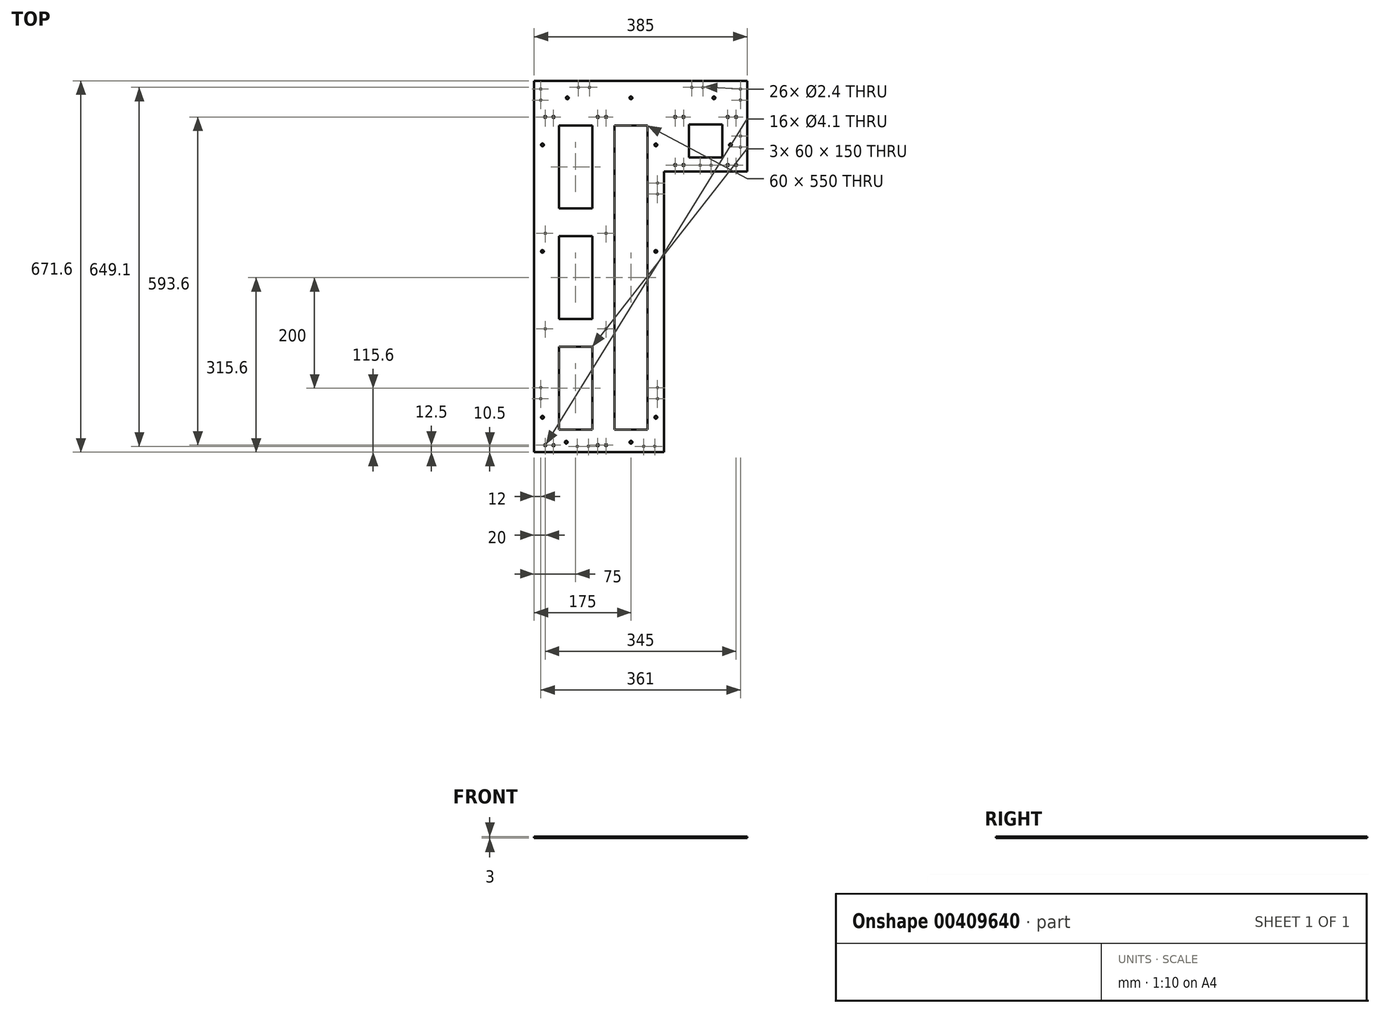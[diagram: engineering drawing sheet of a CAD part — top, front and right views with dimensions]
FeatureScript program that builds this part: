
annotation { "Feature Type Name" : "Feature", "Feature Type Description" : "" }
export const myFeature = defineFeature(function(context is Context, id is Id, definition is map)
    precondition{}
    {
        {
            var Q0;
            Q0=qCreatedBy(makeId("Top.planeOp"),FACE);
            var sketch = newSketch(context, id + "F0", { "sketchPlane" : qUnion([Q0])});
            skLineSegment(sketch, "E0.bottom", {"start": v(192.5, -53) * mm, "end": v(-192.5, -53) * mm});
            skLineSegment(sketch, "E0.top", {"start": v(192.5, 53) * mm, "end": v(-192.5, 53) * mm});
            skLineSegment(sketch, "E0.left", {"start": v(192.5, -53) * mm, "end": v(192.5, 53) * mm});
            skLineSegment(sketch, "E0.right", {"start": v(-192.5, -53) * mm, "end": v(-192.5, 53) * mm});
            skPoint(sketch, "E0.middle", {"position": v(0, 0) * mm});
            skCircle(sketch, "E1", {"center": v(-172.5, 43.5) * mm, "radius": 2.05 * mm});
            skCircle(sketch, "E2", {"center": v(-157.5, 43.5) * mm, "radius": 2.05 * mm});
            skLineSegment(sketch, "E3", {"start": v(-42.5, 73.43) * mm, "end": v(-42.5, -580.65) * mm, "construction": true});
            skLineSegment(sketch, "E4", {"start": v(42.5, 94.16) * mm, "end": v(42.5, -111.22) * mm, "construction": true});
            skCircle(sketch, "E5", {"center": v(-77.5, 43.5) * mm, "radius": 2.05 * mm});
            skCircle(sketch, "E6", {"center": v(-62.5, 43.5) * mm, "radius": 2.05 * mm});
            skCircle(sketch, "E7", {"center": v(62.5, 43.5) * mm, "radius": 2.05 * mm});
            skCircle(sketch, "E8", {"center": v(77.5, 43.5) * mm, "radius": 2.05 * mm});
            skCircle(sketch, "E9", {"center": v(157.5, 43.5) * mm, "radius": 2.05 * mm});
            skCircle(sketch, "E10", {"center": v(172.5, 43.5) * mm, "radius": 2.05 * mm});
            skLineSegment(sketch, "E11", {"start": v(202.9, -33.92) * mm, "end": v(25.15, -33.92) * mm, "construction": true});
            skCircle(sketch, "E12", {"center": v(172.5, -43.42) * mm, "radius": 2.05 * mm});
            skCircle(sketch, "E13", {"center": v(157.5, -43.42) * mm, "radius": 2.05 * mm});
            skCircle(sketch, "E14", {"center": v(62.5, -43.42) * mm, "radius": 2.05 * mm});
            skCircle(sketch, "E15", {"center": v(77.5, -43.42) * mm, "radius": 2.05 * mm});
            skLineSegment(sketch, "E16.bottom", {"start": v(-192.5, -53) * mm, "end": v(42.5, -53) * mm});
            skLineSegment(sketch, "E16.top", {"start": v(-192.5, -559.6) * mm, "end": v(42.5, -559.6) * mm});
            skLineSegment(sketch, "E16.left", {"start": v(-192.5, -53) * mm, "end": v(-192.5, -559.6) * mm});
            skLineSegment(sketch, "E16.right", {"start": v(42.5, -53) * mm, "end": v(42.5, -559.6) * mm});
            skLineSegment(sketch, "E17", {"start": v(-218.51, -539.6) * mm, "end": v(119.99, -539.6) * mm, "construction": true});
            skCircle(sketch, "E18", {"center": v(-172.5, -550.1) * mm, "radius": 2.05 * mm});
            skCircle(sketch, "E19", {"center": v(-157.5, -550.1) * mm, "radius": 2.05 * mm});
            skCircle(sketch, "E20", {"center": v(-77.5, -550.1) * mm, "radius": 2.05 * mm});
            skCircle(sketch, "E21", {"center": v(-62.5, -550.1) * mm, "radius": 2.05 * mm});
            skLineSegment(sketch, "E22", {"start": v(-117.5, 57.85) * mm, "end": v(-117.5, 33.54) * mm, "construction": true});
            skLineSegment(sketch, "E23", {"start": v(-153.12, 33) * mm, "end": v(-174.42, 33) * mm, "construction": true});
            skCircle(sketch, "E24", {"center": v(-172.5, -167) * mm, "radius": 1.2 * mm});
            skLineSegment(sketch, "E25", {"start": v(-176.5, -137.08) * mm, "end": v(-176.5, -144.67) * mm, "construction": true});
            skCircle(sketch, "E26", {"center": v(-172.5, -339.6) * mm, "radius": 1.2 * mm});
            skCircle(sketch, "E27", {"center": v(-62.5, -167) * mm, "radius": 1.2 * mm});
            skCircle(sketch, "E28", {"center": v(-62.5, -339.6) * mm, "radius": 1.2 * mm});
            skCircle(sketch, "E29", {"center": v(-177.5, -199.6) * mm, "radius": 2.5 * mm});
            skCircle(sketch, "E30", {"center": v(-134.5, -544.6) * mm, "radius": 2.5 * mm});
            skLineSegment(sketch, "E31.top", {"start": v(-192.5, -562.6) * mm, "end": v(42.5, -562.6) * mm});
            skLineSegment(sketch, "E31.left", {"start": v(-192.5, -559.6) * mm, "end": v(-192.5, -562.6) * mm});
            skLineSegment(sketch, "E31.right", {"start": v(42.5, -559.6) * mm, "end": v(42.5, -562.6) * mm});
            skCircle(sketch, "E32", {"center": v(-177.5, -499.6) * mm, "radius": 2.5 * mm});
            skCircle(sketch, "E33", {"center": v(-177.5, -7) * mm, "radius": 2.5 * mm});
            skCircle(sketch, "E34", {"center": v(27.5, -199.6) * mm, "radius": 2.5 * mm});
            skCircle(sketch, "E35", {"center": v(-17.5, -544.6) * mm, "radius": 2.5 * mm});
            skCircle(sketch, "E36", {"center": v(27.5, -499.6) * mm, "radius": 2.5 * mm});
            skCircle(sketch, "E37", {"center": v(27.5, -7) * mm, "radius": 2.5 * mm});
            skCircle(sketch, "E38", {"center": v(-132.5, 78) * mm, "radius": 2.5 * mm});
            skCircle(sketch, "E39", {"center": v(132.5, 78) * mm, "radius": 2.5 * mm});
            skCircle(sketch, "E40", {"center": v(-17.5, 78) * mm, "radius": 2.5 * mm});
            skLineSegment(sketch, "E41.bottom", {"start": v(42.5, -53) * mm, "end": v(192.5, -53) * mm});
            skLineSegment(sketch, "E41.top", {"start": v(42.5, -55) * mm, "end": v(192.5, -55) * mm});
            skLineSegment(sketch, "E41.left", {"start": v(42.5, -53) * mm, "end": v(42.5, -55) * mm});
            skLineSegment(sketch, "E41.right", {"start": v(192.5, -53) * mm, "end": v(192.5, -55) * mm});
            skLineSegment(sketch, "E42", {"start": v(-192.5, 53) * mm, "end": v(-192.5, 109) * mm});
            skLineSegment(sketch, "E43", {"start": v(-192.5, 109) * mm, "end": v(192.5, 109) * mm});
            skLineSegment(sketch, "E44", {"start": v(192.5, 109) * mm, "end": v(192.5, 53) * mm});
            skCircle(sketch, "E45", {"center": v(162.5, -7) * mm, "radius": 2.5 * mm});
            skSolve(sketch);
        }
        {
            var Q0;
            Q0 = qSketchRegion(id + "F0", true);
            extrude(context, id + "F1", {"entities" : qUnion([Q0]), "depth" : 3 * mm});
        }
        {
            var Q0;
            Q0=makeQuery(id+"F1.opExtrude","CAP_FACE",FACE,{"disambiguationData":[OSD([sQuery(id+"F0.wireOp",EDGE,"E0.bottom"),sQuery(id+"F0.wireOp",EDGE,"E0.top"),sQuery(id+"F0.wireOp",EDGE,"E0.left"),sQuery(id+"F0.wireOp",EDGE,"E0.right"),sQuery(id+"F0.wireOp",EDGE,"E1"),sQuery(id+"F0.wireOp",EDGE,"E2"),sQuery(id+"F0.wireOp",EDGE,"E5"),sQuery(id+"F0.wireOp",EDGE,"E6"),sQuery(id+"F0.wireOp",EDGE,"E7"),sQuery(id+"F0.wireOp",EDGE,"E8"),sQuery(id+"F0.wireOp",EDGE,"E9"),sQuery(id+"F0.wireOp",EDGE,"E10"),sQuery(id+"F0.wireOp",EDGE,"E12"),sQuery(id+"F0.wireOp",EDGE,"E13"),sQuery(id+"F0.wireOp",EDGE,"E14"),sQuery(id+"F0.wireOp",EDGE,"E15"),sQuery(id+"F0.wireOp",EDGE,"E16.top"),sQuery(id+"F0.wireOp",EDGE,"E16.left"),sQuery(id+"F0.wireOp",EDGE,"E16.right"),sQuery(id+"F0.wireOp",EDGE,"E18"),sQuery(id+"F0.wireOp",EDGE,"E19"),sQuery(id+"F0.wireOp",EDGE,"E20"),sQuery(id+"F0.wireOp",EDGE,"E21")])],"isStart":false});
            var sketch = newSketch(context, id + "F2", { "sketchPlane" : qUnion([Q0])});
            skLineSegment(sketch, "E46.bottom", {"start": v(-87.5, -122) * mm, "end": v(-147.5, -122) * mm});
            skLineSegment(sketch, "E46.top", {"start": v(-87.5, 28) * mm, "end": v(-147.5, 28) * mm});
            skLineSegment(sketch, "E46.left", {"start": v(-87.5, -122) * mm, "end": v(-87.5, 28) * mm});
            skLineSegment(sketch, "E46.right", {"start": v(-147.5, -122) * mm, "end": v(-147.5, 28) * mm});
            skPoint(sketch, "E46.middle", {"position": v(-117.5, -47) * mm});
            skLineSegment(sketch, "E47.bottom", {"start": v(-87.5, -172) * mm, "end": v(-147.5, -172) * mm});
            skLineSegment(sketch, "E47.top", {"start": v(-87.5, -322) * mm, "end": v(-147.5, -322) * mm});
            skLineSegment(sketch, "E47.left", {"start": v(-87.5, -172) * mm, "end": v(-87.5, -322) * mm});
            skLineSegment(sketch, "E47.right", {"start": v(-147.5, -172) * mm, "end": v(-147.5, -322) * mm});
            skPoint(sketch, "E47.middle", {"position": v(-117.5, -247) * mm});
            skLineSegment(sketch, "E48", {"start": v(-117.5, 70.25) * mm, "end": v(-117.5, -57.76) * mm, "construction": true});
            skLineSegment(sketch, "E49", {"start": v(117.5, 72.9) * mm, "end": v(117.5, -109.15) * mm, "construction": true});
            skLineSegment(sketch, "E50.bottom", {"start": v(147.5, -30) * mm, "end": v(87.5, -30) * mm});
            skLineSegment(sketch, "E50.top", {"start": v(147.5, 30) * mm, "end": v(87.5, 30) * mm});
            skLineSegment(sketch, "E50.left", {"start": v(147.5, -30) * mm, "end": v(147.5, 30) * mm});
            skLineSegment(sketch, "E50.right", {"start": v(87.5, -30) * mm, "end": v(87.5, 30) * mm});
            skPoint(sketch, "E50.middle", {"position": v(117.5, 0) * mm});
            skLineSegment(sketch, "E51.bottom", {"start": v(-87.5, -372) * mm, "end": v(-147.5, -372) * mm});
            skLineSegment(sketch, "E51.top", {"start": v(-87.5, -522) * mm, "end": v(-147.5, -522) * mm});
            skLineSegment(sketch, "E51.left", {"start": v(-87.5, -372) * mm, "end": v(-87.5, -522) * mm});
            skLineSegment(sketch, "E51.right", {"start": v(-147.5, -372) * mm, "end": v(-147.5, -522) * mm});
            skPoint(sketch, "E51.middle", {"position": v(-117.5, -447) * mm});
            skLineSegment(sketch, "E52", {"start": v(-42.5, 117.64) * mm, "end": v(-42.5, -137.41) * mm, "construction": true});
            skLineSegment(sketch, "E53.bottom", {"start": v(-47.5, 28) * mm, "end": v(12.5, 28) * mm});
            skLineSegment(sketch, "E53.top", {"start": v(-47.5, -522) * mm, "end": v(12.5, -522) * mm});
            skLineSegment(sketch, "E53.left", {"start": v(-47.5, 28) * mm, "end": v(-47.5, -522) * mm});
            skLineSegment(sketch, "E53.right", {"start": v(12.5, 28) * mm, "end": v(12.5, -522) * mm});
            skSolve(sketch);
        }
        {
            var Q0;
            Q0 = qSketchRegion(id + "F2", true);
            extrude(context, id + "F3", {"entities" : qUnion([Q0]), "operationType" : NewBodyOperationType.REMOVE, "oppositeDirection" : true, "depth" : 25 * mm});
        }
        {
            var Q0;
            Q0=makeQuery(id+"F2O8r8H572E9jEw_1.boolean.opBoolean","MERGE",FACE,{"derivedFrom":[makeQuery(id+"F1.opExtrude","CAP_FACE",FACE,{"disambiguationData":[OSD([sQuery(id+"F0.wireOp",EDGE,"E0.top"),sQuery(id+"F0.wireOp",EDGE,"E0.left"),sQuery(id+"F0.wireOp",EDGE,"E0.right"),sQuery(id+"F0.wireOp",EDGE,"E1"),sQuery(id+"F0.wireOp",EDGE,"E2"),sQuery(id+"F0.wireOp",EDGE,"E5"),sQuery(id+"F0.wireOp",EDGE,"E6"),sQuery(id+"F0.wireOp",EDGE,"E7"),sQuery(id+"F0.wireOp",EDGE,"E8"),sQuery(id+"F0.wireOp",EDGE,"E9"),sQuery(id+"F0.wireOp",EDGE,"E10"),sQuery(id+"F0.wireOp",EDGE,"E12"),sQuery(id+"F0.wireOp",EDGE,"E13"),sQuery(id+"F0.wireOp",EDGE,"E14"),sQuery(id+"F0.wireOp",EDGE,"E15"),sQuery(id+"F0.wireOp",EDGE,"E16.left"),sQuery(id+"F0.wireOp",EDGE,"E16.right"),sQuery(id+"F0.wireOp",EDGE,"E18"),sQuery(id+"F0.wireOp",EDGE,"E19"),sQuery(id+"F0.wireOp",EDGE,"E20"),sQuery(id+"F0.wireOp",EDGE,"E21"),sQuery(id+"F0.wireOp",EDGE,"E24"),sQuery(id+"F0.wireOp",EDGE,"E26"),sQuery(id+"F0.wireOp",EDGE,"E27"),sQuery(id+"F0.wireOp",EDGE,"E28"),sQuery(id+"F0.wireOp",EDGE,"E29"),sQuery(id+"F0.wireOp",EDGE,"E30"),sQuery(id+"F0.wireOp",EDGE,"E31.top"),sQuery(id+"F0.wireOp",EDGE,"E31.left"),sQuery(id+"F0.wireOp",EDGE,"E31.right"),sQuery(id+"F0.wireOp",EDGE,"E32"),sQuery(id+"F0.wireOp",EDGE,"E33"),sQuery(id+"F0.wireOp",EDGE,"E34"),sQuery(id+"F0.wireOp",EDGE,"E35"),sQuery(id+"F0.wireOp",EDGE,"E36"),sQuery(id+"F0.wireOp",EDGE,"E37"),sQuery(id+"F0.wireOp",EDGE,"E38"),sQuery(id+"F0.wireOp",EDGE,"E39"),sQuery(id+"F0.wireOp",EDGE,"TjULq03c-Gpqh-KJec-qWmQ-0YuIlEzygd5B"),sQuery(id+"F0.wireOp",EDGE,"lCEzzgQS-Qvkz-X3D3-LDLk-qSDPH7AwNQJv"),sQuery(id+"F0.wireOp",EDGE,"E40"),sQuery(id+"F0.wireOp",EDGE,"E41.top"),sQuery(id+"F0.wireOp",EDGE,"E41.right")])],"isStart":false}),makeQuery(id+"F2O8r8H572E9jEw_1.opExtrude","CAP_FACE",FACE,{"disambiguationData":[OSD([sQuery(id+"FIaY4WBdf4dioWf_1.wireOp",EDGE,"mXuLmiP2-nhxb-6Rn9-Rc8G-rbgXLuEv7Aki.bottom"),sQuery(id+"FIaY4WBdf4dioWf_1.wireOp",EDGE,"mXuLmiP2-nhxb-6Rn9-Rc8G-rbgXLuEv7Aki.top"),sQuery(id+"FIaY4WBdf4dioWf_1.wireOp",EDGE,"mXuLmiP2-nhxb-6Rn9-Rc8G-rbgXLuEv7Aki.left"),sQuery(id+"FIaY4WBdf4dioWf_1.wireOp",EDGE,"mXuLmiP2-nhxb-6Rn9-Rc8G-rbgXLuEv7Aki.right")])],"isStart":false})]});
            var sketch = newSketch(context, id + "F4", { "sketchPlane" : qUnion([Q0])});
            skCircle(sketch, "E54", {"center": v(-180.5, 94) * mm, "radius": 1.2 * mm});
            skCircle(sketch, "E55", {"center": v(-180.5, 74) * mm, "radius": 1.2 * mm});
            skCircle(sketch, "E56", {"center": v(-180.5, -446) * mm, "radius": 1.2 * mm});
            skCircle(sketch, "E57", {"center": v(-180.5, -466) * mm, "radius": 1.2 * mm});
            skCircle(sketch, "E58", {"center": v(30.5, -446) * mm, "radius": 1.2 * mm});
            skCircle(sketch, "E59", {"center": v(30.5, -466) * mm, "radius": 1.2 * mm});
            skCircle(sketch, "E60", {"center": v(30.5, -76) * mm, "radius": 1.2 * mm});
            skCircle(sketch, "E61", {"center": v(30.5, -96) * mm, "radius": 1.2 * mm});
            skCircle(sketch, "E62", {"center": v(180.5, 94) * mm, "radius": 1.2 * mm});
            skCircle(sketch, "E63", {"center": v(180.5, 74) * mm, "radius": 1.2 * mm});
            skCircle(sketch, "E64", {"center": v(180.5, 9) * mm, "radius": 1.2 * mm});
            skCircle(sketch, "E65", {"center": v(180.5, -11) * mm, "radius": 1.2 * mm});
            skCircle(sketch, "E66", {"center": v(-114.5, -552.1) * mm, "radius": 1.2 * mm});
            skCircle(sketch, "E67", {"center": v(-94.5, -552.1) * mm, "radius": 1.2 * mm});
            skCircle(sketch, "E68", {"center": v(5.5, -552.1) * mm, "radius": 1.2 * mm});
            skCircle(sketch, "E69", {"center": v(25.5, -552.1) * mm, "radius": 1.2 * mm});
            skCircle(sketch, "E70", {"center": v(-112.5, 97) * mm, "radius": 1.2 * mm});
            skCircle(sketch, "E71", {"center": v(-92.5, 97) * mm, "radius": 1.2 * mm});
            skCircle(sketch, "E72", {"center": v(92.5, 97) * mm, "radius": 1.2 * mm});
            skCircle(sketch, "E73", {"center": v(112.5, 97) * mm, "radius": 1.2 * mm});
            skCircle(sketch, "E74", {"center": v(107.5, -43.8) * mm, "radius": 1.2 * mm});
            skCircle(sketch, "E75", {"center": v(127.5, -43.8) * mm, "radius": 1.2 * mm});
            skSolve(sketch);
        }
        {
            var Q0;
            Q0 = qSketchRegion(id + "F4", true);
            extrude(context, id + "F5", {"entities" : qUnion([Q0]), "operationType" : NewBodyOperationType.REMOVE, "oppositeDirection" : true, "depth" : 25 * mm});
        }
    });
